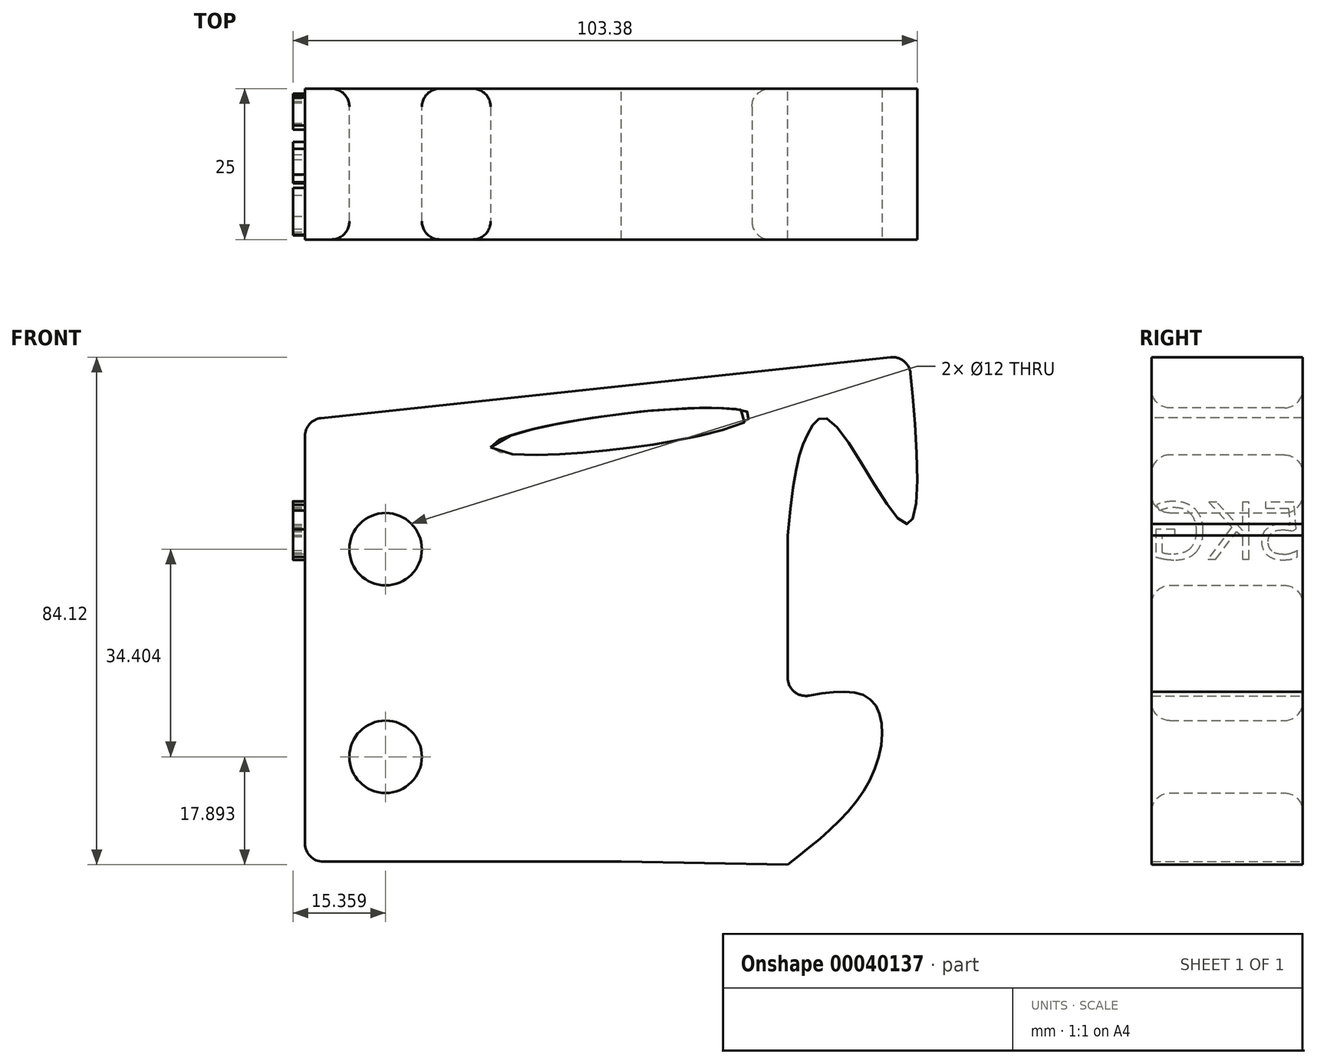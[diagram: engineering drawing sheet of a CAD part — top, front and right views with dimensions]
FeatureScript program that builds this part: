
annotation { "Feature Type Name" : "Feature", "Feature Type Description" : "" }
export const myFeature = defineFeature(function(context is Context, id is Id, definition is map)
    precondition{}
    {
        {
            var Q0;
            Q0=qCreatedBy(makeId("Front.planeOp"),FACE);
            var sketch = newSketch(context, id + "F0", { "sketchPlane" : qUnion([Q0])});
            skLineSegment(sketch, "E0.top", {"start": v(-52.38, -34.36) * mm, "end": v(0, -34.36) * mm});
            skLineSegment(sketch, "E0.left", {"start": v(-52.38, 38.86) * mm, "end": v(-52.38, -34.36) * mm});
            skLineSegment(sketch, "E0.right", {"start": v(27.56, 19.73) * mm, "end": v(27.56, -7.57) * mm});
            skLineSegment(sketch, "E1", {"start": v(-52.38, 38.86) * mm, "end": v(47.6, 49.56) * mm});
            skFitSpline(sketch, "E2", {"points": [v(47.6, 49.56) * mm, v(47.6, 21.64) * mm, v(34.44, 38.86) * mm, v(31.1, 36.95) * mm, v(27.56, 19.73) * mm], "startDerivative": vector(3.75, -37.29) * mm, "endDerivative": vector(-10.45, -117.15) * mm});
            skEllipse(sketch, "E3", {"center": v(0, 36.95) * mm, "majorRadius": 21.8 * mm, "minorRadius": 2.87 * mm, "majorAxis": v(-1, -0.12)});
            skLineSegment(sketch, "E4", {"start": v(0, -34.36) * mm, "end": v(27.56, -34.87) * mm});
            skPoint(sketch, "E5.1.internal.snap0", {"position": v(27.56, -7.57) * mm});
            skFitSpline(sketch, "E5", {"points": [v(27.56, -7.57) * mm, v(41.37, -7.57) * mm, v(41.61, -19.97) * mm, v(27.56, -34.87) * mm], "startDerivative": vector(53.14, 11.4) * mm, "endDerivative": vector(-44.5, -34.93) * mm});
            skCircle(sketch, "E6", {"center": v(-39.02, 17.43) * mm, "radius": 6 * mm});
            skCircle(sketch, "E7", {"center": v(-39.02, -16.98) * mm, "radius": 6 * mm});
            skSolve(sketch);
        }
        {
            var Q0;
            Q0=makeQuery(id+"F0.imprint","IMPRINT",FACE,{"disambiguationData":[TD([[makeQuery(id+"F0.imprint","IMPRINT",EDGE,{"derivedFrom":sQuery(id+"F0.wireOp",EDGE,"E0.top")}),1.0]])]});
            extrude(context, id + "F1", {"entities" : qUnion([Q0]), "depth" : 25 * mm});
        }
        {
            var Q0;
            Q0=makeQuery(id+"F1.opExtrude","CAP_EDGE",EDGE,{"disambiguationData":[OSD([sQuery(id+"F0.wireOp",EDGE,"E3")])],"isStart":false});
            var Q1;
            Q1=makeQuery(id+"F1.opExtrude","CAP_EDGE",EDGE,{"disambiguationData":[OSD([sQuery(id+"F0.wireOp",EDGE,"E3")])],"isStart":true});
            var Q2;
            Q2=makeQuery(id+"F1.opExtrude","SWEPT_EDGE",EDGE,{"disambiguationData":[OSD([sQuery(id+"F0.wireOp",EDGE,"E0.left"),sQuery(id+"F0.wireOp",EDGE,"E1")])]});
            var Q3;
            Q3=makeQuery(id+"F1.opExtrude","SWEPT_EDGE",EDGE,{"disambiguationData":[OSD([sQuery(id+"F0.wireOp",EDGE,"E0.top"),sQuery(id+"F0.wireOp",EDGE,"E0.left")])]});
            var Q4;
            Q4=makeQuery(id+"F1.opExtrude","SWEPT_EDGE",EDGE,{"disambiguationData":[OSD([sQuery(id+"F0.wireOp",EDGE,"E0.right"),sQuery(id+"F0.wireOp",EDGE,"E5")])]});
            var Q5;
            Q5=makeQuery(id+"F1.opExtrude","SWEPT_EDGE",EDGE,{"disambiguationData":[OSD([sQuery(id+"F0.wireOp",EDGE,"E1"),sQuery(id+"F0.wireOp",EDGE,"E2")])]});
            var Q6;
            Q6=makeQuery(id+"F1.opExtrude","CAP_EDGE",EDGE,{"disambiguationData":[OSD([sQuery(id+"F0.wireOp",EDGE,"E6")])],"isStart":true});
            var Q7;
            Q7=makeQuery(id+"F1.opExtrude","CAP_EDGE",EDGE,{"disambiguationData":[OSD([sQuery(id+"F0.wireOp",EDGE,"E7")])],"isStart":true});
            var Q8;
            Q8=makeQuery(id+"F1.opExtrude","CAP_EDGE",EDGE,{"disambiguationData":[OSD([sQuery(id+"F0.wireOp",EDGE,"E6")])],"isStart":false});
            var Q9;
            Q9=makeQuery(id+"F1.opExtrude","CAP_EDGE",EDGE,{"disambiguationData":[OSD([sQuery(id+"F0.wireOp",EDGE,"E7")])],"isStart":false});
            fillet(context, id + "F2", {"entities" : qUnion([Q0, Q1, Q2, Q3, Q4, Q5, Q6, Q7, Q8, Q9]), "radius" : 3 * mm, "tangentPropagation" : true, "allowEdgeOverflow" : false});
        }
        {
            var Q0;
            Q0=makeQuery(id+"F1.opExtrude","SWEPT_FACE",FACE,{"disambiguationData":[OSD([sQuery(id+"F0.wireOp",EDGE,"E0.left")])]});
            var sketch = newSketch(context, id + "F3", { "sketchPlane" : qUnion([Q0])});
            skText(sketch, "E8", { "text": "5KG\n", "fontName": "OpenSans-Regular.ttf"});
            const initialGuessF3  = {"E8": [0, 0.01578, 1, 0, 0.00952]};
            skSetInitialGuess(sketch, initialGuessF3);
            skSolve(sketch);
        }
        {
            var Q0;
            Q0 = qSketchRegion(id + "F3", true);
            extrude(context, id + "F4", {"entities" : qUnion([Q0]), "operationType" : NewBodyOperationType.ADD, "depth" : 2 * mm});
        }
    });
